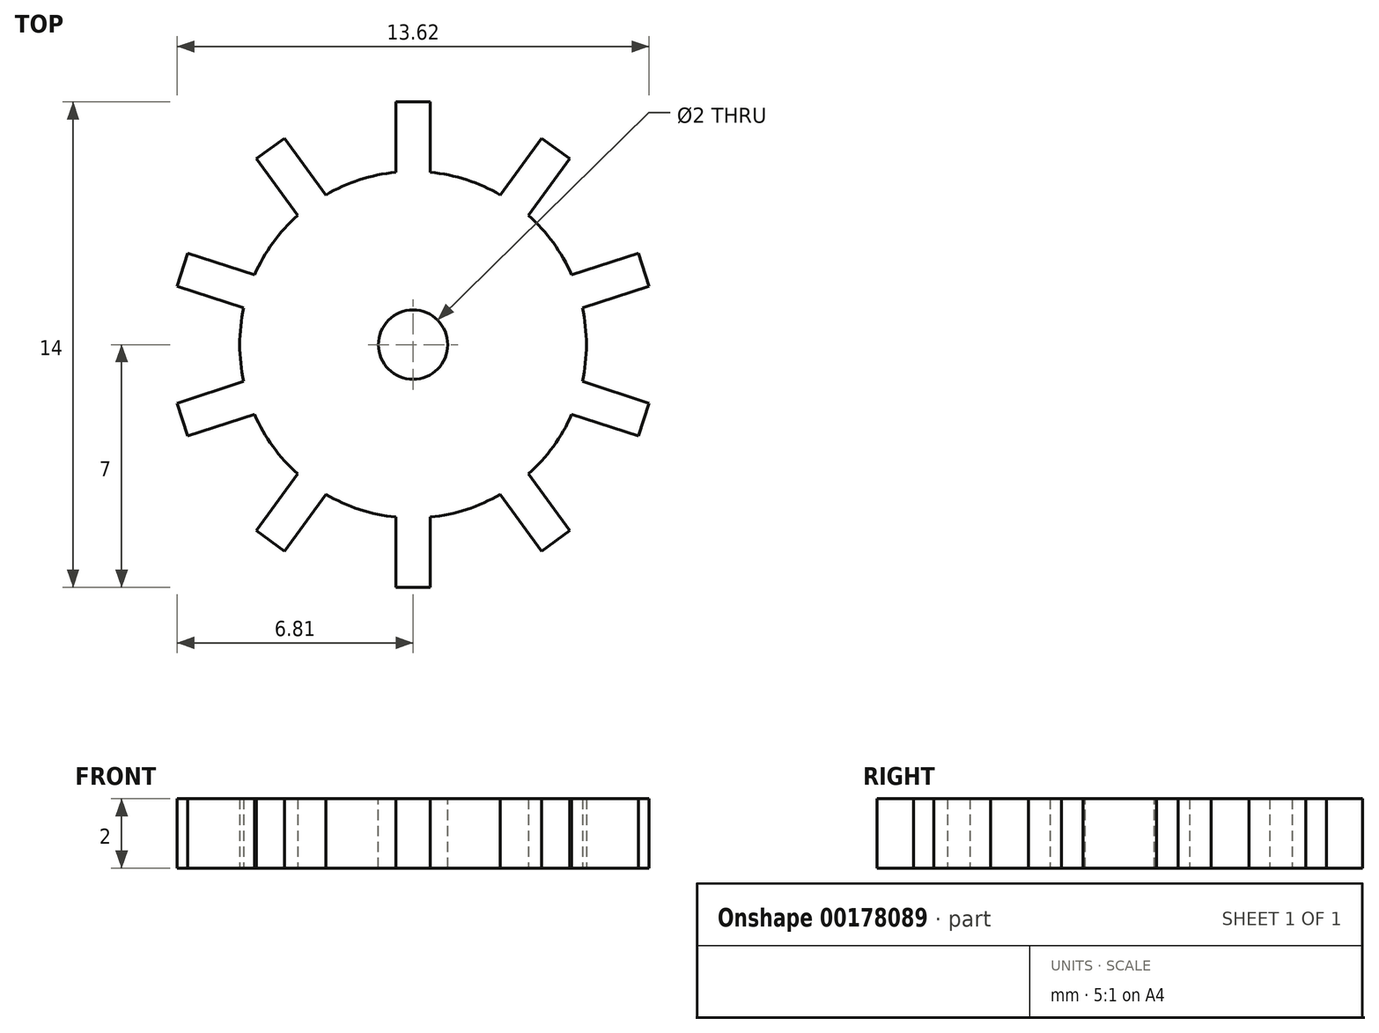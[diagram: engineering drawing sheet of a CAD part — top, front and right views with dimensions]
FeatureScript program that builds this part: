
annotation { "Feature Type Name" : "Feature", "Feature Type Description" : "" }
export const myFeature = defineFeature(function(context is Context, id is Id, definition is map)
    precondition{}
    {
        {
            var Q0;
            Q0=qCreatedBy(makeId("Top.planeOp"),FACE);
            var sketch = newSketch(context, id + "F0", { "sketchPlane" : qUnion([Q0])});
            skCircle(sketch, "E0", {"center": v(0, 0) * mm, "radius": 5 * mm});
            skLineSegment(sketch, "E1", {"start": v(0, 0) * mm, "end": v(0, 5) * mm, "construction": true});
            skLineSegment(sketch, "E2", {"start": v(0, 7) * mm, "end": v(-0.5, 7) * mm});
            skLineSegment(sketch, "E3", {"start": v(-0.5, 7) * mm, "end": v(-0.5, 4.97) * mm});
            skLineSegment(sketch, "E4.MirrorCS", {"start": v(0, 7) * mm, "end": v(0.5, 7) * mm});
            skLineSegment(sketch, "E5.MirrorCS", {"start": v(0.5, 7) * mm, "end": v(0.5, 4.97) * mm});
            skLineSegment(sketch, "E6.1.0", {"start": v(-4.52, 5.37) * mm, "end": v(-3.33, 3.73) * mm});
            skLineSegment(sketch, "E6.1.1", {"start": v(-4.11, 5.66) * mm, "end": v(-4.52, 5.37) * mm});
            skLineSegment(sketch, "E6.1.2", {"start": v(-4.11, 5.66) * mm, "end": v(-3.7, 5.96) * mm});
            skLineSegment(sketch, "E6.1.3", {"start": v(-3.7, 5.96) * mm, "end": v(-2.52, 4.32) * mm});
            skLineSegment(sketch, "E6.2.0", {"start": v(-6.81, 1.69) * mm, "end": v(-4.89, 1.06) * mm});
            skLineSegment(sketch, "E6.2.1", {"start": v(-6.66, 2.16) * mm, "end": v(-6.81, 1.69) * mm});
            skLineSegment(sketch, "E6.2.2", {"start": v(-6.66, 2.16) * mm, "end": v(-6.5, 2.64) * mm});
            skLineSegment(sketch, "E6.2.3", {"start": v(-6.5, 2.64) * mm, "end": v(-4.58, 2.01) * mm});
            skLineSegment(sketch, "E6.3.0", {"start": v(-6.5, -2.64) * mm, "end": v(-4.58, -2.01) * mm});
            skLineSegment(sketch, "E6.3.1", {"start": v(-6.66, -2.16) * mm, "end": v(-6.5, -2.64) * mm});
            skLineSegment(sketch, "E6.3.2", {"start": v(-6.66, -2.16) * mm, "end": v(-6.81, -1.69) * mm});
            skLineSegment(sketch, "E6.3.3", {"start": v(-6.81, -1.69) * mm, "end": v(-4.89, -1.06) * mm});
            skLineSegment(sketch, "E6.4.0", {"start": v(-3.7, -5.96) * mm, "end": v(-2.52, -4.32) * mm});
            skLineSegment(sketch, "E6.4.1", {"start": v(-4.11, -5.66) * mm, "end": v(-3.7, -5.96) * mm});
            skLineSegment(sketch, "E6.4.2", {"start": v(-4.11, -5.66) * mm, "end": v(-4.52, -5.37) * mm});
            skLineSegment(sketch, "E6.4.3", {"start": v(-4.52, -5.37) * mm, "end": v(-3.33, -3.73) * mm});
            skLineSegment(sketch, "E6.5.0", {"start": v(0.5, -7) * mm, "end": v(0.5, -4.97) * mm});
            skLineSegment(sketch, "E6.5.1", {"start": v(0, -7) * mm, "end": v(0.5, -7) * mm});
            skLineSegment(sketch, "E6.5.2", {"start": v(0, -7) * mm, "end": v(-0.5, -7) * mm});
            skLineSegment(sketch, "E6.5.3", {"start": v(-0.5, -7) * mm, "end": v(-0.5, -4.97) * mm});
            skLineSegment(sketch, "E7.2.6.0", {"start": v(4.52, -5.37) * mm, "end": v(3.33, -3.73) * mm});
            skLineSegment(sketch, "E7.3.6.0", {"start": v(4.11, -5.66) * mm, "end": v(4.52, -5.37) * mm});
            skLineSegment(sketch, "E7.6.6.0", {"start": v(4.11, -5.66) * mm, "end": v(3.7, -5.96) * mm});
            skLineSegment(sketch, "E7.9.6.0", {"start": v(3.7, -5.96) * mm, "end": v(2.52, -4.32) * mm});
            skLineSegment(sketch, "E7.2.7.0", {"start": v(6.81, -1.69) * mm, "end": v(4.89, -1.06) * mm});
            skLineSegment(sketch, "E7.3.7.0", {"start": v(6.66, -2.16) * mm, "end": v(6.81, -1.69) * mm});
            skLineSegment(sketch, "E7.6.7.0", {"start": v(6.66, -2.16) * mm, "end": v(6.5, -2.64) * mm});
            skLineSegment(sketch, "E7.9.7.0", {"start": v(6.5, -2.64) * mm, "end": v(4.58, -2.01) * mm});
            skLineSegment(sketch, "E7.2.8.0", {"start": v(6.5, 2.64) * mm, "end": v(4.58, 2.01) * mm});
            skLineSegment(sketch, "E7.3.8.0", {"start": v(6.66, 2.16) * mm, "end": v(6.5, 2.64) * mm});
            skLineSegment(sketch, "E7.6.8.0", {"start": v(6.66, 2.16) * mm, "end": v(6.81, 1.69) * mm});
            skLineSegment(sketch, "E7.9.8.0", {"start": v(6.81, 1.69) * mm, "end": v(4.89, 1.06) * mm});
            skLineSegment(sketch, "E7.2.9.0", {"start": v(3.7, 5.96) * mm, "end": v(2.52, 4.32) * mm});
            skLineSegment(sketch, "E7.3.9.0", {"start": v(4.11, 5.66) * mm, "end": v(3.7, 5.96) * mm});
            skLineSegment(sketch, "E7.6.9.0", {"start": v(4.11, 5.66) * mm, "end": v(4.52, 5.37) * mm});
            skLineSegment(sketch, "E7.9.9.0", {"start": v(4.52, 5.37) * mm, "end": v(3.33, 3.73) * mm});
            skSolve(sketch);
        }
        {
            var Q0;
            Q0=qSketchRegion(id+"F0",true);
            extrude(context, id + "F1", {"entities" : qUnion([Q0]), "depth" : 2 * mm});
        }
        {
            var Q0;
            Q0=makeQuery(id+"F1.opExtrude","CAP_FACE",FACE,{"disambiguationData":[OSD([sQuery(id+"F0.wireOp",EDGE,"E0"),sQuery(id+"F0.wireOp",EDGE,"E2"),sQuery(id+"F0.wireOp",EDGE,"E3"),sQuery(id+"F0.wireOp",EDGE,"E4.MirrorCS"),sQuery(id+"F0.wireOp",EDGE,"E5.MirrorCS"),sQuery(id+"F0.wireOp",EDGE,"E6.1.0"),sQuery(id+"F0.wireOp",EDGE,"E6.1.1"),sQuery(id+"F0.wireOp",EDGE,"E6.1.2"),sQuery(id+"F0.wireOp",EDGE,"E6.1.3"),sQuery(id+"F0.wireOp",EDGE,"E6.2.0"),sQuery(id+"F0.wireOp",EDGE,"E6.2.1"),sQuery(id+"F0.wireOp",EDGE,"E6.2.2"),sQuery(id+"F0.wireOp",EDGE,"E6.2.3"),sQuery(id+"F0.wireOp",EDGE,"E6.3.0"),sQuery(id+"F0.wireOp",EDGE,"E6.3.1"),sQuery(id+"F0.wireOp",EDGE,"E6.3.2"),sQuery(id+"F0.wireOp",EDGE,"E6.3.3"),sQuery(id+"F0.wireOp",EDGE,"E6.4.0"),sQuery(id+"F0.wireOp",EDGE,"E6.4.1"),sQuery(id+"F0.wireOp",EDGE,"E6.4.2"),sQuery(id+"F0.wireOp",EDGE,"E6.4.3"),sQuery(id+"F0.wireOp",EDGE,"E6.5.0"),sQuery(id+"F0.wireOp",EDGE,"E6.5.1"),sQuery(id+"F0.wireOp",EDGE,"E6.5.2"),sQuery(id+"F0.wireOp",EDGE,"E6.5.3")])],"isStart":false});
            var sketch = newSketch(context, id + "F2", { "sketchPlane" : qUnion([Q0])});
            skCircle(sketch, "E8", {"center": v(0, 0) * mm, "radius": 1 * mm});
            skSolve(sketch);
        }
        {
            var Q0;
            Q0=qSketchRegion(id+"F2",true);
            extrude(context, id + "F3", {"entities" : qUnion([Q0]), "operationType" : NewBodyOperationType.REMOVE, "endBound" : BoundingType.THROUGH_ALL, "oppositeDirection" : true, "depth" : 25 * mm});
        }
    });
